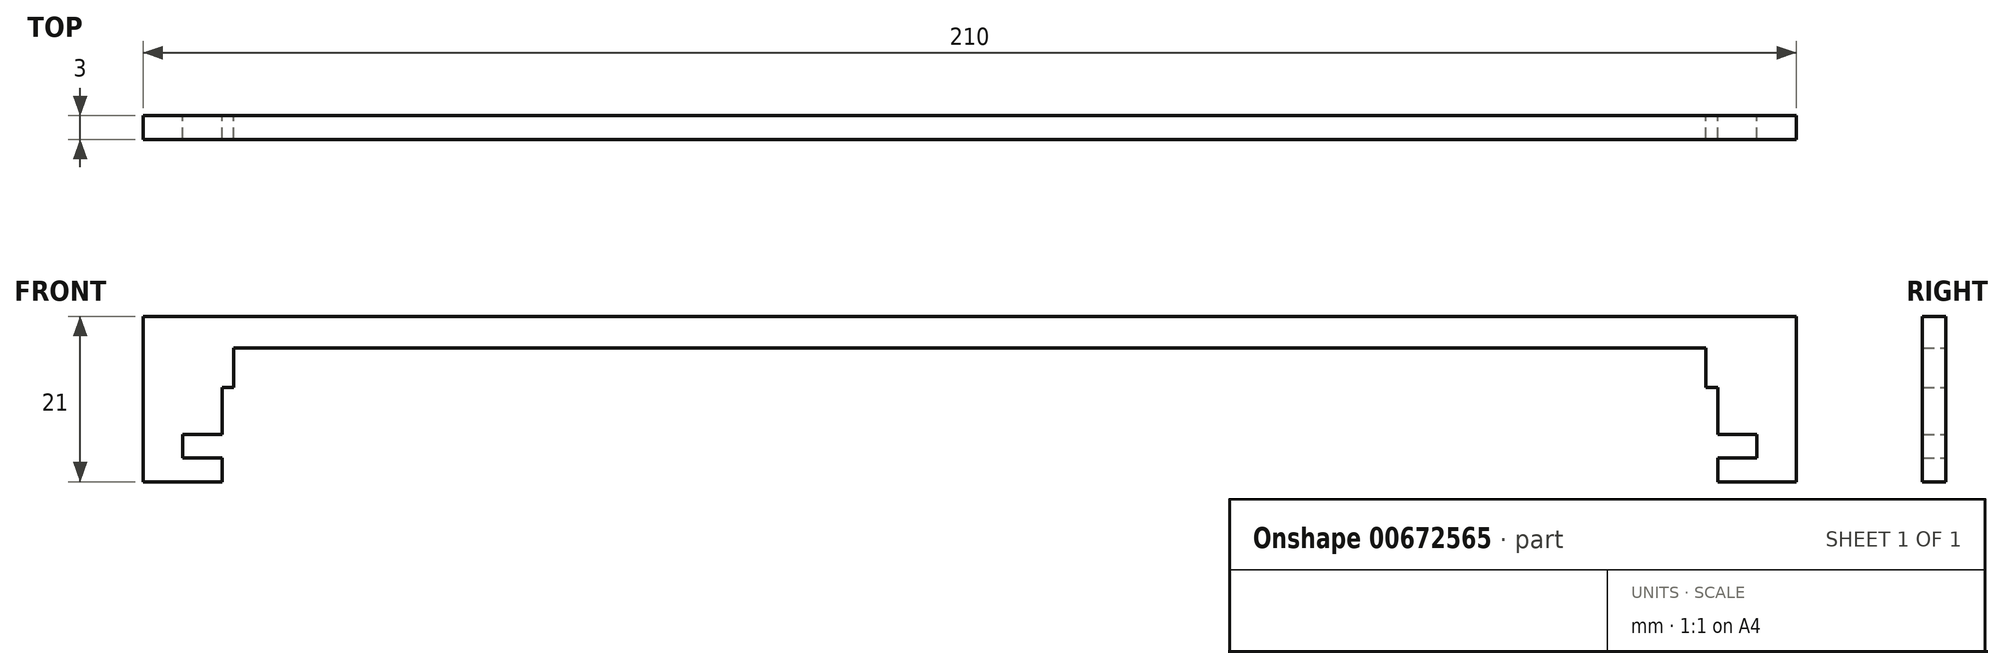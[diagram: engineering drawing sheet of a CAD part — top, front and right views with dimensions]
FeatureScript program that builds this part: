
annotation { "Feature Type Name" : "Feature", "Feature Type Description" : "" }
export const myFeature = defineFeature(function(context is Context, id is Id, definition is map)
    precondition{}
    {
        {
            var Q0;
            Q0=qCreatedBy(makeId("Front.planeOp"),FACE);
            var sketch = newSketch(context, id + "F0", { "sketchPlane" : qUnion([Q0])});
            skPoint(sketch, "E0.middle", {"position": v(0, 0) * mm});
            skLineSegment(sketch, "E1.left", {"start": v(-100, -7) * mm, "end": v(-100, -4) * mm});
            skLineSegment(sketch, "E2.left", {"start": v(-95, 2) * mm, "end": v(-95, -4) * mm});
            skLineSegment(sketch, "E3.left", {"start": v(-95, -10) * mm, "end": v(-95, -7) * mm});
            skLineSegment(sketch, "E4", {"start": v(-105, -10) * mm, "end": v(-95, -10) * mm});
            skLineSegment(sketch, "E5", {"start": v(-95, -7) * mm, "end": v(-100, -7) * mm});
            skLineSegment(sketch, "E6", {"start": v(-100, -4) * mm, "end": v(-95, -4) * mm});
            skLineSegment(sketch, "E7", {"start": v(-95, 2) * mm, "end": v(-93.5, 2) * mm});
            skLineSegment(sketch, "E8.MirrorCS", {"start": v(100, -7) * mm, "end": v(100, -4) * mm});
            skLineSegment(sketch, "E9.MirrorCS", {"start": v(95, -10) * mm, "end": v(95, -7) * mm});
            skLineSegment(sketch, "E10.MirrorCS", {"start": v(95, 2) * mm, "end": v(93.5, 2) * mm});
            skLineSegment(sketch, "E11.MirrorCS", {"start": v(95, 2) * mm, "end": v(95, -4) * mm});
            skLineSegment(sketch, "E12.MirrorCS", {"start": v(95, -7) * mm, "end": v(100, -7) * mm});
            skLineSegment(sketch, "E13.MirrorCS", {"start": v(100, -4) * mm, "end": v(95, -4) * mm});
            skLineSegment(sketch, "E14", {"start": v(93.5, 7) * mm, "end": v(-93.5, 7) * mm});
            skLineSegment(sketch, "E15", {"start": v(-105, 11) * mm, "end": v(105, 11) * mm});
            skLineSegment(sketch, "E16", {"start": v(-105, -10) * mm, "end": v(-105, 11) * mm});
            skLineSegment(sketch, "E17", {"start": v(95, -10) * mm, "end": v(105, -10) * mm});
            skLineSegment(sketch, "E18", {"start": v(105, 11) * mm, "end": v(105, -10) * mm});
            skLineSegment(sketch, "E19", {"start": v(93.5, 7) * mm, "end": v(93.5, 2) * mm});
            skLineSegment(sketch, "E20", {"start": v(-93.5, 2) * mm, "end": v(-93.5, 7) * mm});
            skSolve(sketch);
        }
        {
            var Q0;
            Q0=makeQuery(id+"F0.imprint","IMPRINT",FACE,{"disambiguationData":[TD([[makeQuery(id+"F0.imprint","IMPRINT",EDGE,{"derivedFrom":sQuery(id+"F0.wireOp",EDGE,"E1.left")}),1.0]])]});
            extrude(context, id + "F1", {"entities" : qUnion([Q0]), "depth" : 3 * mm, "offsetDistance" : 25 * mm});
        }
    });
